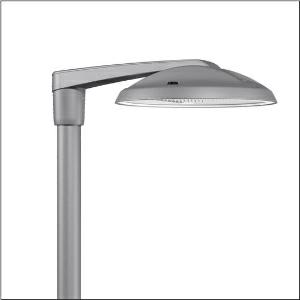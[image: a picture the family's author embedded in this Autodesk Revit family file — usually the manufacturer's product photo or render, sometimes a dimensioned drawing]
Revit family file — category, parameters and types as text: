
# Revit family: dl_r__50_iq_mini___st1_0a_5xa248d31v08le_d4cd
name_source: partatom
category: Lighting Fixtures
units: mm (PartAtom-declared; Revit-internal decimal feet)

## family parameters
Cut with Voids When Loaded = No
Host = Face
Light Source = No
Part Type = Normal
Room Calculation Point = No
Round Connector Dimension = Use Diameter
Shared = No

## types (1)
- --- (1 x LED, 10390 lm, 66 W, 3000K)
    Apparent Load = 66 VA
    CIE Flux Codes = 37 72 97 100 100
    Color Rendering = 70
    Color Temperature = 3000K
    Default Elevation = 1800 mm
    Description = DL® 50 iQ mini, mast luminaire, primary light control with lens, of PMMA, primary optical cover: cover, of toughened safety glass, transparent, light distribution: ST1.0a, light emission: direct distribution, primary light characteristic: asymmetric, installation type: post-top, side-entry, LED, High Power LED, rated luminous flux: 10.390lm, luminous efficacy: 157lm/W, light colour: 730, colour temperature: 3000K, control: optimised constant luminous flux control (CLO 2.0), Desk-Remote (wireless, voltage-free reading and setting of iQ features in the workshop via application-optimized NFC function/RFID function), Light-Fading, Smart-Wire, Night-Set, Lumen-Switch, Temp-Guard, Auto-Match, Street-Remote, presetting dimming logarithmic, mains connection: 230..240V, AC, 50/60Hz, connection cable pre-assembled, cable length: 8,5m, start of lifetime: 66W, end of service life: 69W, reduction: 30W, luminaire housing, of diecast aluminium, powder-coated, Siteco® metallic grey (DB 702S), inclination adjustable: 0°, 5°, 10° (post-top) | 0°, -5°, -10°, -15° (side-entry), please order mast post-top element or mast side-entry element separately, diameter: 500mm, height: 115mm, post-top: for spigot size d x l = 76 x 100mm; with reducer (optional accessory) 60 x 100mm | side-entry: for spigot size d x l = 60 x 100mm; with reducer (optional accessory) 42 x 100mm, Smart Interface above, protection rating (complete): IP66, insulation class (complete): insulation class II (safety insulation), certification: CE, ENEC, VDE, impact resistance: IK08, permissible operating ambient temperature for outdoor applications: -25..+40°C, standard-compliant lighting for roads and squares, packaging unit: 1 piece

Light Distribution: ST1.0a
    Height = 115 mm
    Lamp = 1 x LED
    Lamp Light Flux = 10390 lm
    Lamp Power = 66 W
    Lamp count = 1
    Length = 500 mm
    Luminous efficacy = 157 lm/W
    Manufacturer = Siteco
    ModVariant = No
    Model = 5XA248D31V08LE
    Number of Poles = 1
    OnlyDefault = Yes
    Power Factor = 1
    Product Name = DL® 50 iQ mini | ST1.0a
    Product group = mast luminaire | pylon top
    ProductGroupID = 6100
    Protection Class = Protection class II
    Protection Degree = IP 66
    RLX_Detail_Level = 1
    RLX_Emergency_Light_Flux = 0 lm
    RLX_Emergency_Type = 0
    RLX_Emergency_Type_DB = No
    RlxData = <blob elided: 106421 chars, md5=4a8403bb>
    Socket = socket
    Standby Power = 0 W
    System Light Flux = 10390 lm
    System Power = 66 W
    Type Comments = factory setting: luminous flux: 100 % | dim-lin: 254 | 691 mA
    Type Image = l_1251788.jpg
    URL = http://relux.com
    VarID = @adj_026283
    Voltage = 0 V
    Weight = 0.00 kg
    Width = 0 mm  [stored 0 ft]

note: [stored X ft] marks values corroborated as IEEE doubles in the binary element streams (Revit-internal decimal feet)

## geometry (parser evidence)
native form markers: Blend x4, Sweep x9
no freeform markers — native parametric forms only
